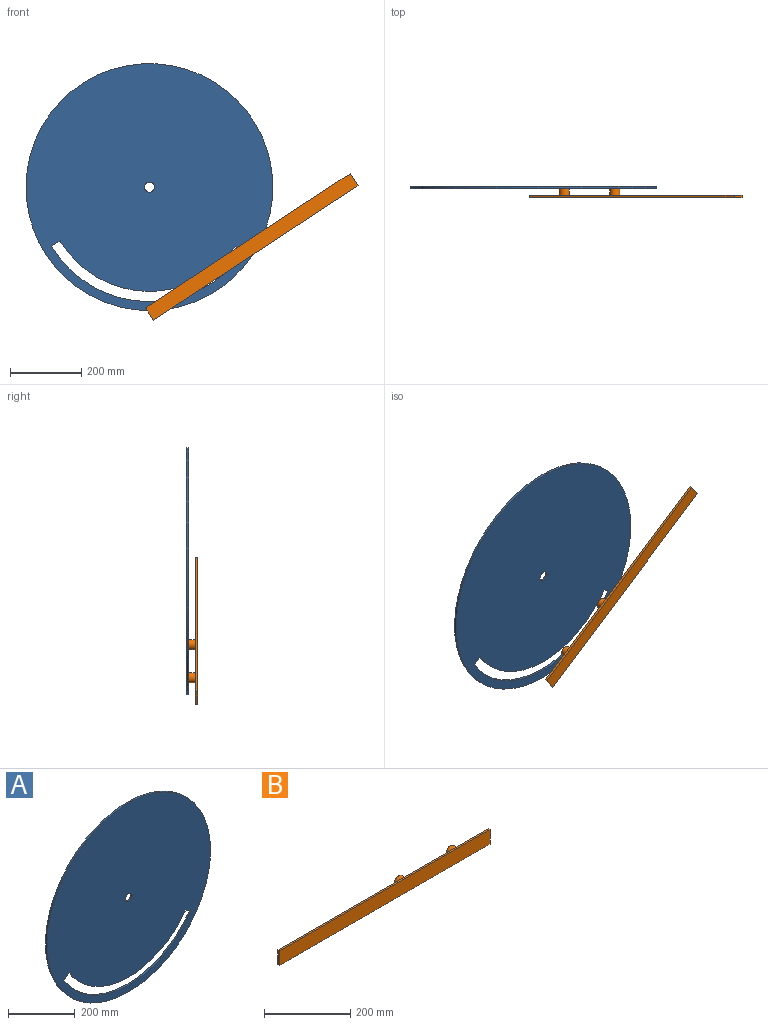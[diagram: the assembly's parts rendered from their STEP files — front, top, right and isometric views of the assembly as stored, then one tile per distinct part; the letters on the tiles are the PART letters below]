
ASSEMBLY  parts=2 mates=1
PART A: 8 faces, bbox 694x6.4x694 mm
  f0: cylinder r=293.03mm len=492.02mm, axis (0,1,0), area 3711.1mm2, adj f1,f5,f6,f7
  f1: plane 23.5x16.25mm, normal (-0.57,0,-0.82), area 181.5mm2, adj f0,f2,f6,f7
  f2: cylinder r=321.61mm len=540mm, axis (0,1,0), area 4073mm2, adj f1,f5,f6,f7
  f3: cylinder r=347.01mm len=694.02mm, axis (0,1,0), area 13845mm2, adj f6,f7
  f4: cylinder r=14.29mm len=28.58mm, axis (0,1,0), area 570mm2, adj f6,f7
  f5: plane 24.48x14.74mm, normal (0.52,0,-0.86), area 181.5mm2, adj f0,f2,f6,f7
  f6: plane 694.02x694.02mm, normal (0,-1,0), area 360138.1mm2, adj f0,f1,f2,f3,f4,f5
  f7: plane 694.02x694.02mm, normal (0,1,0), area 360138.1mm2, adj f0,f1,f2,f3,f4,f5
PART B: 10 faces, bbox 687.8x25.4x40.8 mm
  f0: plane 40.85x6.35mm, normal (-1,0,0), area 259.4mm2, adj f1,f3,f4,f5
  f1: plane 687.81x6.35mm, normal (0,0,1), area 4367.6mm2, adj f0,f2,f4,f5
  f2: plane 40.85x6.35mm, normal (1,0,0), area 259.4mm2, adj f1,f3,f4,f5
  f3: plane 687.81x6.35mm, normal (0,0,-1), area 4367.6mm2, adj f0,f2,f4,f5
  f4: plane 687.81x40.85mm, normal (0,1,0), area 26811.9mm2, adj f0,f1,f2,f3,f6,f8
  f5: plane 687.81x40.85mm, normal (0,-1,0), area 28094.5mm2, adj f0,f1,f2,f3
  f6: cylinder r=14.29mm len=28.58mm, axis (0,-1,0), area 1710.1mm2, adj f4,f7
  f7: plane 28.58x28.58mm, normal (0,1,0), area 641.3mm2, adj f6
  f8: cylinder r=14.29mm len=28.58mm, axis (0,-1,0), area 1710.1mm2, adj f4,f9
  f9: plane 28.58x28.58mm, normal (0,1,0), area 641.3mm2, adj f8
PLACE A t=(459.54,168.81,619.15)mm
PLACE B rot(axis=(0,1,0),146.7deg) t=(1388.09,137.06,847.46)mm
MATE pin_slot A.f6 <-> B.f6  axis (0,-1,0) through (724.06,162.46,436.23)mm
